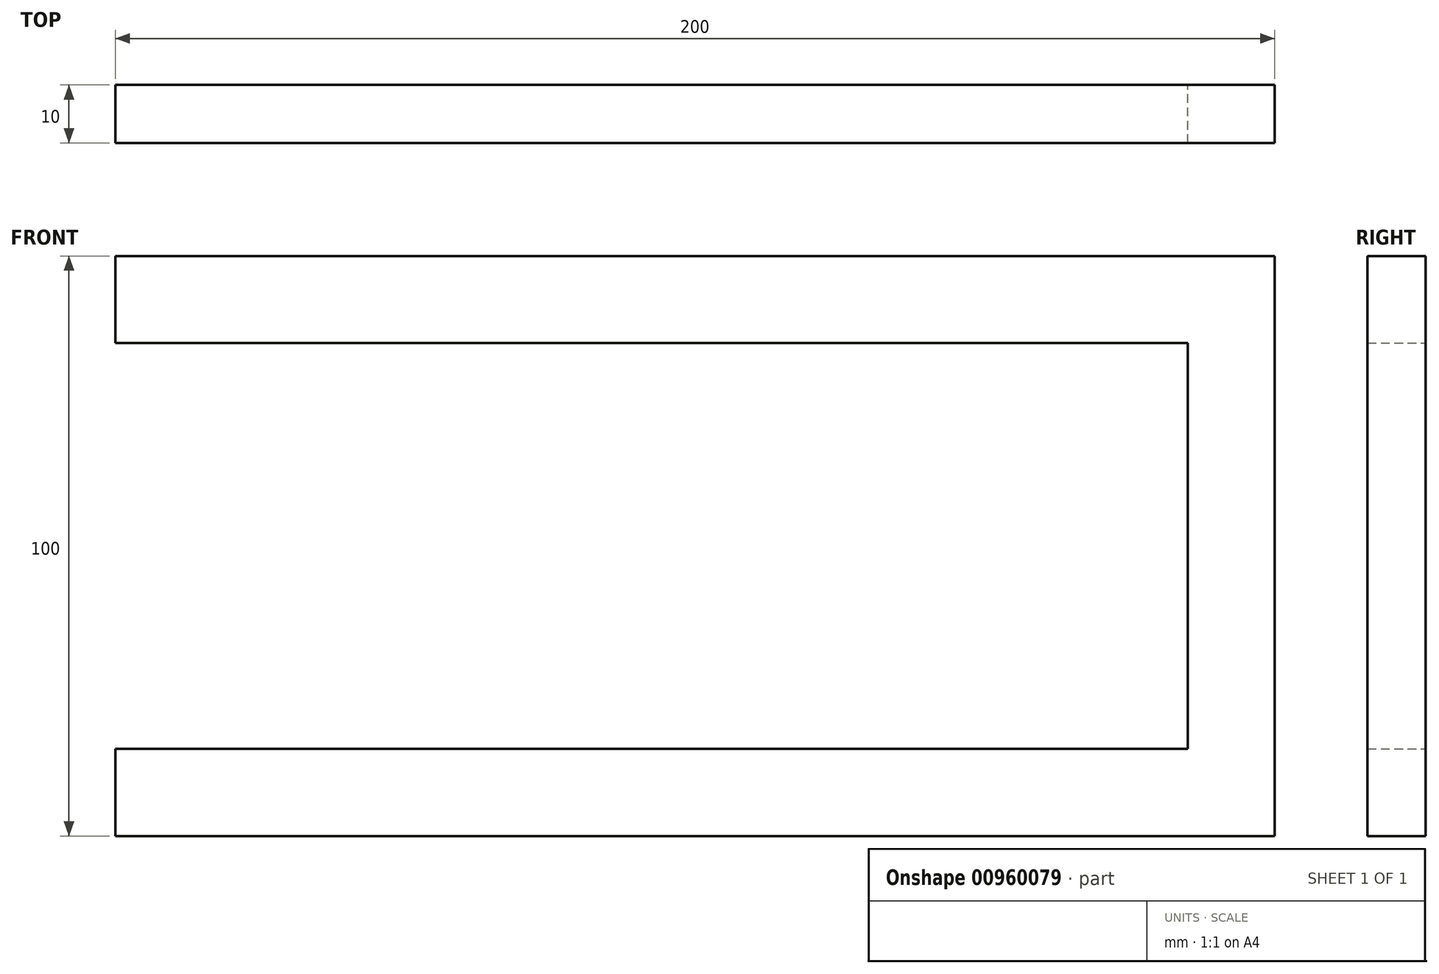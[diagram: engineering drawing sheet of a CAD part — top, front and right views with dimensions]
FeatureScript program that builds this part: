
annotation { "Feature Type Name" : "Feature", "Feature Type Description" : "" }
export const myFeature = defineFeature(function(context is Context, id is Id, definition is map)
    precondition{}
    {
        {
            var Q0;
            Q0=qCreatedBy(makeId("Front.planeOp"),FACE);
            var sketch = newSketch(context, id + "F0", { "sketchPlane" : qUnion([Q0])});
            skLineSegment(sketch, "E0.bottom", {"start": v(-100, 50) * mm, "end": v(100, 50) * mm});
            skLineSegment(sketch, "E0.top", {"start": v(-100, -50) * mm, "end": v(100, -50) * mm});
            skLineSegment(sketch, "E0.left", {"start": v(-100, 50) * mm, "end": v(-100, -50) * mm});
            skLineSegment(sketch, "E0.right", {"start": v(100, 50) * mm, "end": v(100, -50) * mm});
            skPoint(sketch, "E0.middle", {"position": v(0, 0) * mm});
            skLineSegment(sketch, "E1", {"start": v(-85, -35) * mm, "end": v(85, -35) * mm});
            skLineSegment(sketch, "E2", {"start": v(85, -35) * mm, "end": v(85, 35) * mm});
            skLineSegment(sketch, "E3", {"start": v(-85, 35) * mm, "end": v(85, 35) * mm});
            skLineSegment(sketch, "E4", {"start": v(-85, 35) * mm, "end": v(-100, 35) * mm});
            skLineSegment(sketch, "E5", {"start": v(-85, -35) * mm, "end": v(-100, -35) * mm});
            skSolve(sketch);
        }
        {
            var Q0;
            {var subQ3=sQuery(id+"F0.wireOp",EDGE,"E0.bottom");Q0=makeQuery(id+"F0.imprint","IMPRINT",FACE,{"disambiguationData":[TD([[makeQuery(id+"F0.imprint","IMPRINT",EDGE,{"derivedFrom":subQ3}),-1.0]])]});}
            extrude(context, id + "F1", {"entities" : qUnion([Q0]), "depth" : 10 * mm, "offsetDistance" : 25 * mm});
        }
    });
